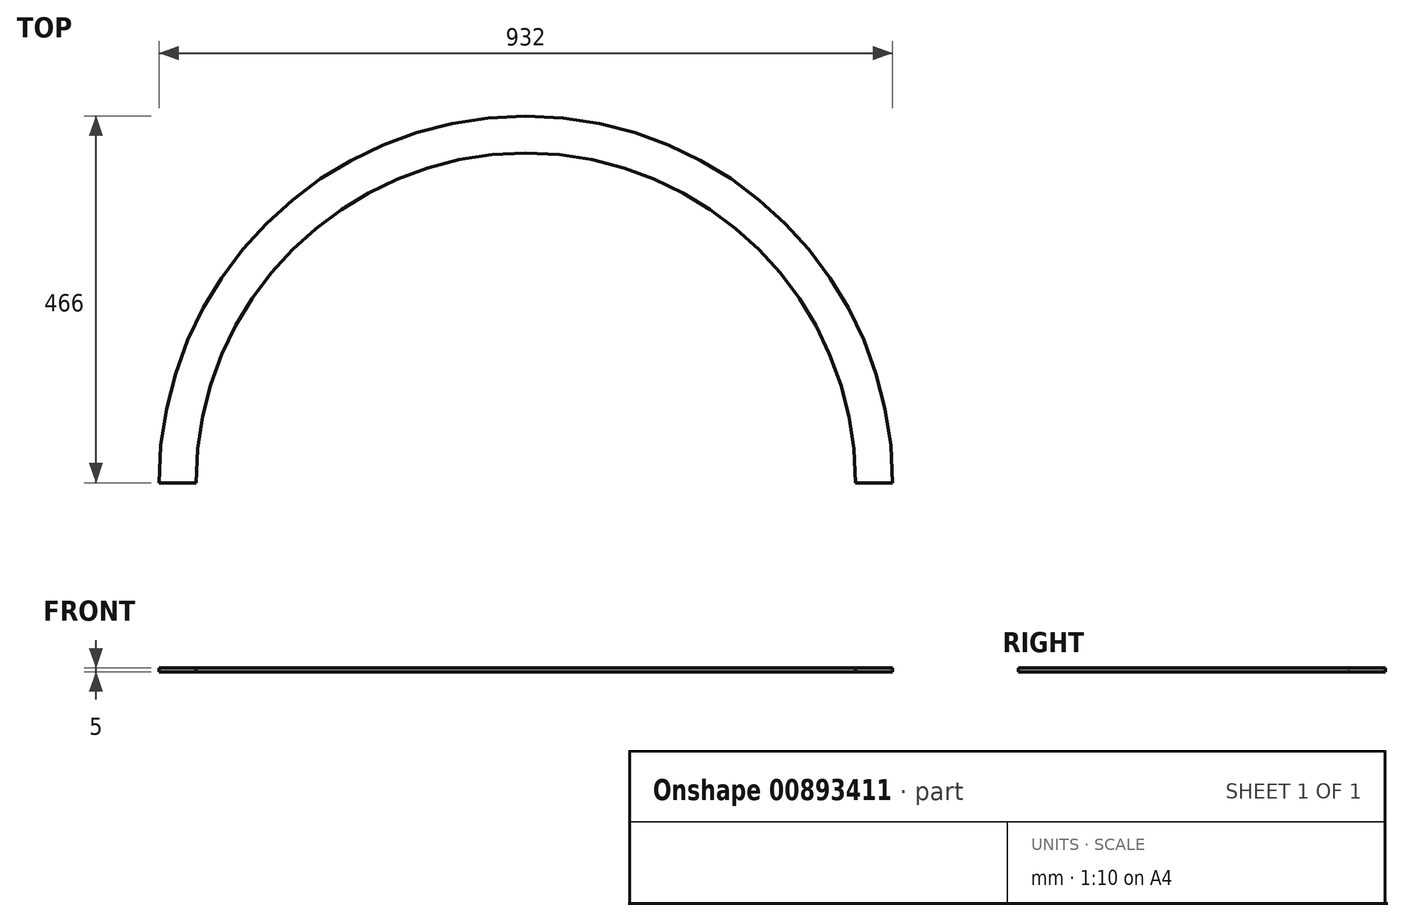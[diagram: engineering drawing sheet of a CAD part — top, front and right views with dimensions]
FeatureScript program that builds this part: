
annotation { "Feature Type Name" : "Feature", "Feature Type Description" : "" }
export const myFeature = defineFeature(function(context is Context, id is Id, definition is map)
    precondition{}
    {
        {
            var Q0;
            Q0=qCreatedBy(makeId("Top.planeOp"),FACE);
            var sketch = newSketch(context, id + "F0", { "sketchPlane" : qUnion([Q0])});
            skArc(sketch, "E0", {"start": v(419, 0) * mm, "mid": v(0, 419) * mm, "end": v(-419, 0) * mm});
            skCircle(sketch, "E1", {"center": v(106.34, 493.72) * mm, "radius": 16 * mm});
            skArc(sketch, "E2", {"start": v(466, 0) * mm, "mid": v(0, 466) * mm, "end": v(-466, 0) * mm});
            skLineSegment(sketch, "E3", {"start": v(419, 0) * mm, "end": v(466, 0) * mm});
            skLineSegment(sketch, "E4", {"start": v(-419, 0) * mm, "end": v(-466, 0) * mm});
            skSolve(sketch);
        }
        {
            var Q0;
            Q0=makeQuery(id+"F0.imprint","IMPRINT",FACE,{"disambiguationData":[TD([[makeQuery(id+"F0.imprint","IMPRINT",EDGE,{"derivedFrom":sQuery(id+"F0.wireOp",EDGE,"E0")}),-1.0]])]});
            extrude(context, id + "F1", {"entities" : qUnion([Q0]), "depth" : 5 * mm, "offsetDistance" : 25 * mm});
        }
    });
